# Revit family: Shower-Showerhead-KOHLER-KATALYST_AIR-K-15994T
name_source: partatom
category: Plumbing Fixtures
revit_build: Autodesk Revit 2017 (Build: 20160225_1515(x64)
units: mm (PartAtom-declared; Revit-internal decimal feet)

## family parameters
Cut with Voids When Loaded = No
Host = Face
OmniClass Number = 23.31.17.00
OmniClass Title = Showers
Part Type = Normal
Room Calculation Point = No
Round Connector Dimension = Use Diameter
Shared = No

## types (6) — shared parameters
ADA Compliant = No
Assembly Code = D2010700
CW Connection = No
Cold Water Inlet = Cold Water Inlet
Date Modified = 09/16/2020
Default Elevation = 0"
Description = AIR SHOWERHEAD rain shower head 14
Drain Included = No
Flow Rate = 0 GPM
HW Connection = Yes
Height = 14"
Hot Water Inlet = Tempered Water Inlet
Length = 2 9/16"
Manufacturer = KOHLER Co.
Master Format 2014 = 22 42 23
Master Format 2014 Name = Residential Showers
Material = Premium Metal Construction
Pressure = 0.00 psi
Product Documentation Link = https://files.kohler.com.cn
Product Name = Katalyst
Product Page URL = https://www.kohler.com.cn
URL = http://www.kohler.com.cn
Vent Connection = No
Waste Connection = No
Waste Water Outlet = Waste Water Outlet
WaterSense Certified = No
Width = 14"

## per-type parameters (varying)
| type | Finish | Model | Type |
| CP-Polished Chrome | Kohler-Metal-CP-Polished_Chrome | K-15994T-CL-CP | 1 |
| AF-Flange Gold | Kohler-Metal-AF-Flange_Gold | K-15994T-CL-AF | 2 |
| BN-Roman Silver | Kohler-Metal-BN-Roman_Silver | K-15994T-CL-BN | 3 |
| SN-Champagne Gold | Kohler-Metal-SN-Champagne_Gold | K-15994T-CL-SN | 4 |
| PGD-Eternal Gold | Kohler-Metal-PGD-Eternal_Gold | K-15994T-CL-PGD | 5 |
| BV-Roman Copper | Kohler-Metal-BV-Roman_Copper | K-15994T-CL-BV | 6 |

## geometry (parser evidence)
native form markers: Sweep x6
no freeform markers — native parametric forms only
